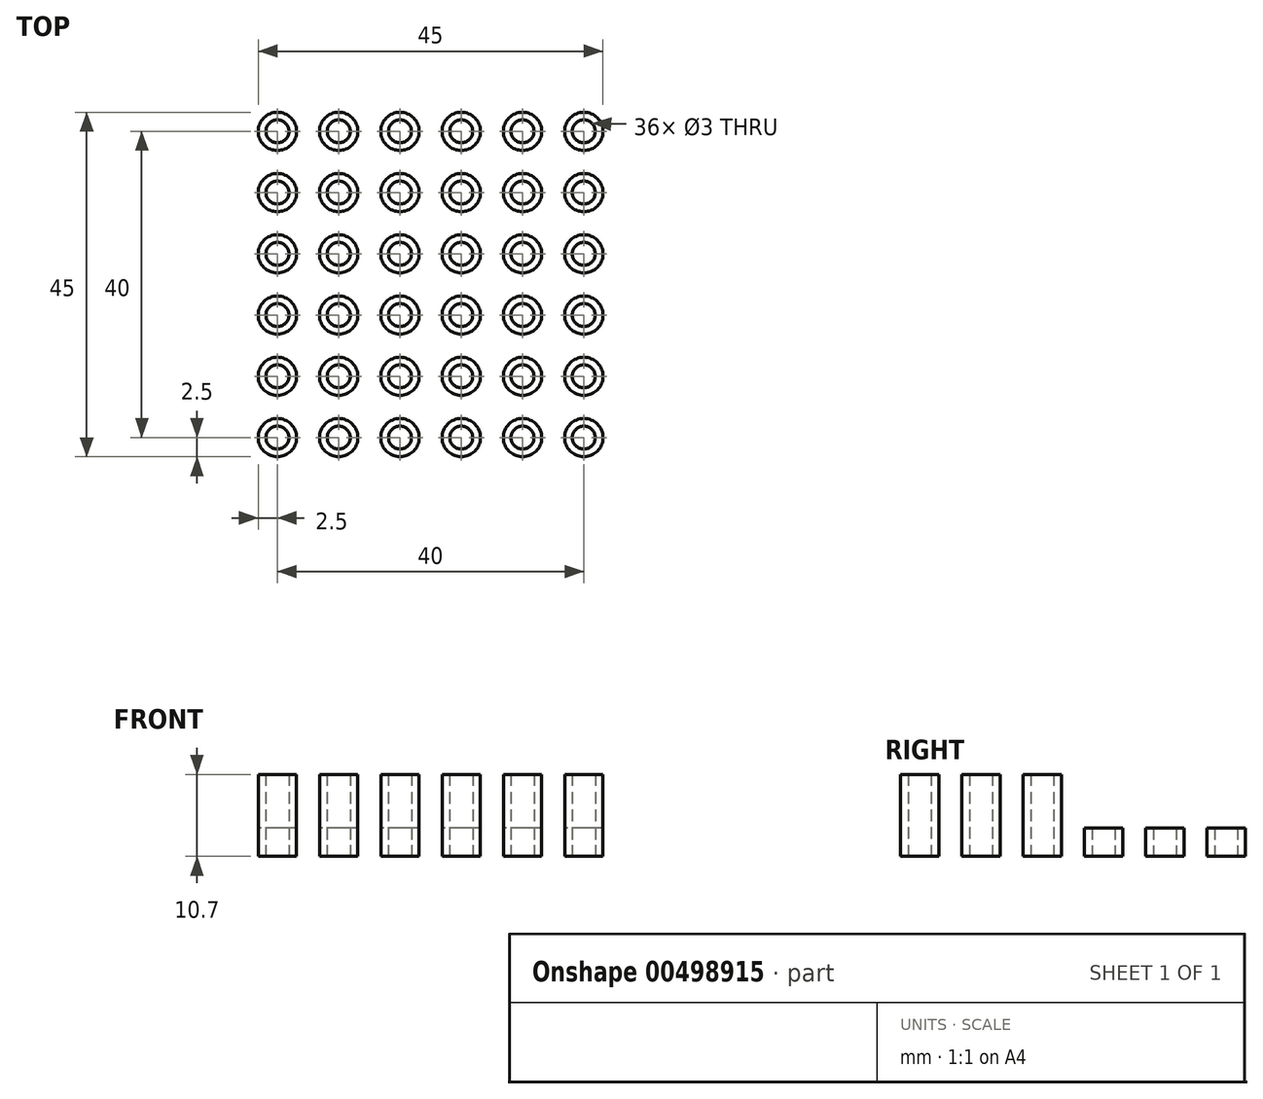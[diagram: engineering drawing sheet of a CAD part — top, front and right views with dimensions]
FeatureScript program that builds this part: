
annotation { "Feature Type Name" : "Feature", "Feature Type Description" : "" }
export const myFeature = defineFeature(function(context is Context, id is Id, definition is map)
    precondition{}
    {
        {
            var Q0;
            Q0=qCreatedBy(makeId("Top.planeOp"),FACE);
            var sketch = newSketch(context, id + "F0", { "sketchPlane" : qUnion([Q0])});
            skCircle(sketch, "E0", {"center": v(-20, -20) * mm, "radius": 1.5 * mm});
            skCircle(sketch, "E1", {"center": v(-20, -20) * mm, "radius": 2.5 * mm});
            skCircle(sketch, "E2.0.1.0", {"center": v(-20, -12) * mm, "radius": 2.5 * mm});
            skCircle(sketch, "E2.0.1.1", {"center": v(-20, -12) * mm, "radius": 1.5 * mm});
            skCircle(sketch, "E2.0.2.0", {"center": v(-20, -4) * mm, "radius": 2.5 * mm});
            skCircle(sketch, "E2.0.2.1", {"center": v(-20, -4) * mm, "radius": 1.5 * mm});
            skCircle(sketch, "E2.0.3.0", {"center": v(-20, 4) * mm, "radius": 2.5 * mm});
            skCircle(sketch, "E2.0.3.1", {"center": v(-20, 4) * mm, "radius": 1.5 * mm});
            skCircle(sketch, "E2.0.4.0", {"center": v(-20, 12) * mm, "radius": 2.5 * mm});
            skCircle(sketch, "E2.0.4.1", {"center": v(-20, 12) * mm, "radius": 1.5 * mm});
            skCircle(sketch, "E2.0.5.0", {"center": v(-20, 20) * mm, "radius": 2.5 * mm});
            skCircle(sketch, "E2.0.5.1", {"center": v(-20, 20) * mm, "radius": 1.5 * mm});
            skCircle(sketch, "E2.1.0.0", {"center": v(-12, -20) * mm, "radius": 2.5 * mm});
            skCircle(sketch, "E2.1.0.1", {"center": v(-12, -20) * mm, "radius": 1.5 * mm});
            skCircle(sketch, "E2.1.1.0", {"center": v(-12, -12) * mm, "radius": 2.5 * mm});
            skCircle(sketch, "E2.1.1.1", {"center": v(-12, -12) * mm, "radius": 1.5 * mm});
            skCircle(sketch, "E2.1.2.0", {"center": v(-12, -4) * mm, "radius": 2.5 * mm});
            skCircle(sketch, "E2.1.2.1", {"center": v(-12, -4) * mm, "radius": 1.5 * mm});
            skCircle(sketch, "E2.1.3.0", {"center": v(-12, 4) * mm, "radius": 2.5 * mm});
            skCircle(sketch, "E2.1.3.1", {"center": v(-12, 4) * mm, "radius": 1.5 * mm});
            skCircle(sketch, "E2.1.4.0", {"center": v(-12, 12) * mm, "radius": 2.5 * mm});
            skCircle(sketch, "E2.1.4.1", {"center": v(-12, 12) * mm, "radius": 1.5 * mm});
            skCircle(sketch, "E2.1.5.0", {"center": v(-12, 20) * mm, "radius": 2.5 * mm});
            skCircle(sketch, "E2.1.5.1", {"center": v(-12, 20) * mm, "radius": 1.5 * mm});
            skCircle(sketch, "E2.2.0.0", {"center": v(-4, -20) * mm, "radius": 2.5 * mm});
            skCircle(sketch, "E2.2.0.1", {"center": v(-4, -20) * mm, "radius": 1.5 * mm});
            skCircle(sketch, "E2.2.1.0", {"center": v(-4, -12) * mm, "radius": 2.5 * mm});
            skCircle(sketch, "E2.2.1.1", {"center": v(-4, -12) * mm, "radius": 1.5 * mm});
            skCircle(sketch, "E2.2.2.0", {"center": v(-4, -4) * mm, "radius": 2.5 * mm});
            skCircle(sketch, "E2.2.2.1", {"center": v(-4, -4) * mm, "radius": 1.5 * mm});
            skCircle(sketch, "E2.2.3.0", {"center": v(-4, 4) * mm, "radius": 2.5 * mm});
            skCircle(sketch, "E2.2.3.1", {"center": v(-4, 4) * mm, "radius": 1.5 * mm});
            skCircle(sketch, "E2.2.4.0", {"center": v(-4, 12) * mm, "radius": 2.5 * mm});
            skCircle(sketch, "E2.2.4.1", {"center": v(-4, 12) * mm, "radius": 1.5 * mm});
            skCircle(sketch, "E2.2.5.0", {"center": v(-4, 20) * mm, "radius": 2.5 * mm});
            skCircle(sketch, "E2.2.5.1", {"center": v(-4, 20) * mm, "radius": 1.5 * mm});
            skCircle(sketch, "E2.3.0.0", {"center": v(4, -20) * mm, "radius": 2.5 * mm});
            skCircle(sketch, "E2.3.0.1", {"center": v(4, -20) * mm, "radius": 1.5 * mm});
            skCircle(sketch, "E2.3.1.0", {"center": v(4, -12) * mm, "radius": 2.5 * mm});
            skCircle(sketch, "E2.3.1.1", {"center": v(4, -12) * mm, "radius": 1.5 * mm});
            skCircle(sketch, "E2.3.2.0", {"center": v(4, -4) * mm, "radius": 2.5 * mm});
            skCircle(sketch, "E2.3.2.1", {"center": v(4, -4) * mm, "radius": 1.5 * mm});
            skCircle(sketch, "E2.3.3.0", {"center": v(4, 4) * mm, "radius": 2.5 * mm});
            skCircle(sketch, "E2.3.3.1", {"center": v(4, 4) * mm, "radius": 1.5 * mm});
            skCircle(sketch, "E2.3.4.0", {"center": v(4, 12) * mm, "radius": 2.5 * mm});
            skCircle(sketch, "E2.3.4.1", {"center": v(4, 12) * mm, "radius": 1.5 * mm});
            skCircle(sketch, "E2.3.5.0", {"center": v(4, 20) * mm, "radius": 2.5 * mm});
            skCircle(sketch, "E2.3.5.1", {"center": v(4, 20) * mm, "radius": 1.5 * mm});
            skCircle(sketch, "E2.4.0.0", {"center": v(12, -20) * mm, "radius": 2.5 * mm});
            skCircle(sketch, "E2.4.0.1", {"center": v(12, -20) * mm, "radius": 1.5 * mm});
            skCircle(sketch, "E2.4.1.0", {"center": v(12, -12) * mm, "radius": 2.5 * mm});
            skCircle(sketch, "E2.4.1.1", {"center": v(12, -12) * mm, "radius": 1.5 * mm});
            skCircle(sketch, "E2.4.2.0", {"center": v(12, -4) * mm, "radius": 2.5 * mm});
            skCircle(sketch, "E2.4.2.1", {"center": v(12, -4) * mm, "radius": 1.5 * mm});
            skCircle(sketch, "E2.4.3.0", {"center": v(12, 4) * mm, "radius": 2.5 * mm});
            skCircle(sketch, "E2.4.3.1", {"center": v(12, 4) * mm, "radius": 1.5 * mm});
            skCircle(sketch, "E2.4.4.0", {"center": v(12, 12) * mm, "radius": 2.5 * mm});
            skCircle(sketch, "E2.4.4.1", {"center": v(12, 12) * mm, "radius": 1.5 * mm});
            skCircle(sketch, "E2.4.5.0", {"center": v(12, 20) * mm, "radius": 2.5 * mm});
            skCircle(sketch, "E2.4.5.1", {"center": v(12, 20) * mm, "radius": 1.5 * mm});
            skCircle(sketch, "E2.5.0.0", {"center": v(20, -20) * mm, "radius": 2.5 * mm});
            skCircle(sketch, "E2.5.0.1", {"center": v(20, -20) * mm, "radius": 1.5 * mm});
            skCircle(sketch, "E2.5.1.0", {"center": v(20, -12) * mm, "radius": 2.5 * mm});
            skCircle(sketch, "E2.5.1.1", {"center": v(20, -12) * mm, "radius": 1.5 * mm});
            skCircle(sketch, "E2.5.2.0", {"center": v(20, -4) * mm, "radius": 2.5 * mm});
            skCircle(sketch, "E2.5.2.1", {"center": v(20, -4) * mm, "radius": 1.5 * mm});
            skCircle(sketch, "E2.5.3.0", {"center": v(20, 4) * mm, "radius": 2.5 * mm});
            skCircle(sketch, "E2.5.3.1", {"center": v(20, 4) * mm, "radius": 1.5 * mm});
            skCircle(sketch, "E2.5.4.0", {"center": v(20, 12) * mm, "radius": 2.5 * mm});
            skCircle(sketch, "E2.5.4.1", {"center": v(20, 12) * mm, "radius": 1.5 * mm});
            skCircle(sketch, "E2.5.5.0", {"center": v(20, 20) * mm, "radius": 2.5 * mm});
            skCircle(sketch, "E2.5.5.1", {"center": v(20, 20) * mm, "radius": 1.5 * mm});
            skLineSegment(sketch, "E2.direction1", {"start": v(-20, -20) * mm, "end": v(-12, -20) * mm, "construction": true});
            skLineSegment(sketch, "E2.direction2", {"start": v(-20, -20) * mm, "end": v(-20, -12) * mm, "construction": true});
            skSolve(sketch);
        }
        {
            var Q0;
            Q0=makeQuery(id+"F0.imprint","IMPRINT",FACE,{"disambiguationData":[TD([[makeQuery(id+"F0.imprint","IMPRINT",EDGE,{"derivedFrom":sQuery(id+"F0.wireOp",EDGE,"E2.0.5.0")}),1.0]])]});
            var Q1;
            Q1=makeQuery(id+"F0.imprint","IMPRINT",FACE,{"disambiguationData":[TD([[makeQuery(id+"F0.imprint","IMPRINT",EDGE,{"derivedFrom":sQuery(id+"F0.wireOp",EDGE,"E2.2.5.0")}),1.0]])]});
            var Q2;
            Q2=makeQuery(id+"F0.imprint","IMPRINT",FACE,{"disambiguationData":[TD([[makeQuery(id+"F0.imprint","IMPRINT",EDGE,{"derivedFrom":sQuery(id+"F0.wireOp",EDGE,"E2.1.5.0")}),1.0]])]});
            var Q3;
            Q3=makeQuery(id+"F0.imprint","IMPRINT",FACE,{"disambiguationData":[TD([[makeQuery(id+"F0.imprint","IMPRINT",EDGE,{"derivedFrom":sQuery(id+"F0.wireOp",EDGE,"E2.3.5.0")}),1.0]])]});
            var Q4;
            Q4=makeQuery(id+"F0.imprint","IMPRINT",FACE,{"disambiguationData":[TD([[makeQuery(id+"F0.imprint","IMPRINT",EDGE,{"derivedFrom":sQuery(id+"F0.wireOp",EDGE,"E2.4.5.0")}),1.0]])]});
            var Q5;
            Q5=makeQuery(id+"F0.imprint","IMPRINT",FACE,{"disambiguationData":[TD([[makeQuery(id+"F0.imprint","IMPRINT",EDGE,{"derivedFrom":sQuery(id+"F0.wireOp",EDGE,"E2.4.4.0")}),1.0]])]});
            var Q6;
            Q6=makeQuery(id+"F0.imprint","IMPRINT",FACE,{"disambiguationData":[TD([[makeQuery(id+"F0.imprint","IMPRINT",EDGE,{"derivedFrom":sQuery(id+"F0.wireOp",EDGE,"E2.3.4.0")}),1.0]])]});
            var Q7;
            Q7=makeQuery(id+"F0.imprint","IMPRINT",FACE,{"disambiguationData":[TD([[makeQuery(id+"F0.imprint","IMPRINT",EDGE,{"derivedFrom":sQuery(id+"F0.wireOp",EDGE,"E2.2.4.0")}),1.0]])]});
            var Q8;
            Q8=makeQuery(id+"F0.imprint","IMPRINT",FACE,{"disambiguationData":[TD([[makeQuery(id+"F0.imprint","IMPRINT",EDGE,{"derivedFrom":sQuery(id+"F0.wireOp",EDGE,"E2.1.4.0")}),1.0]])]});
            var Q9;
            Q9=makeQuery(id+"F0.imprint","IMPRINT",FACE,{"disambiguationData":[TD([[makeQuery(id+"F0.imprint","IMPRINT",EDGE,{"derivedFrom":sQuery(id+"F0.wireOp",EDGE,"E2.5.5.0")}),1.0]])]});
            var Q10;
            Q10=makeQuery(id+"F0.imprint","IMPRINT",FACE,{"disambiguationData":[TD([[makeQuery(id+"F0.imprint","IMPRINT",EDGE,{"derivedFrom":sQuery(id+"F0.wireOp",EDGE,"E2.5.4.0")}),1.0]])]});
            var Q11;
            Q11=makeQuery(id+"F0.imprint","IMPRINT",FACE,{"disambiguationData":[TD([[makeQuery(id+"F0.imprint","IMPRINT",EDGE,{"derivedFrom":sQuery(id+"F0.wireOp",EDGE,"E2.0.4.0")}),1.0]])]});
            var Q12;
            Q12=makeQuery(id+"F0.imprint","IMPRINT",FACE,{"disambiguationData":[TD([[makeQuery(id+"F0.imprint","IMPRINT",EDGE,{"derivedFrom":sQuery(id+"F0.wireOp",EDGE,"E2.0.3.0")}),1.0]])]});
            var Q13;
            Q13=makeQuery(id+"F0.imprint","IMPRINT",FACE,{"disambiguationData":[TD([[makeQuery(id+"F0.imprint","IMPRINT",EDGE,{"derivedFrom":sQuery(id+"F0.wireOp",EDGE,"E2.1.3.0")}),1.0]])]});
            var Q14;
            Q14=makeQuery(id+"F0.imprint","IMPRINT",FACE,{"disambiguationData":[TD([[makeQuery(id+"F0.imprint","IMPRINT",EDGE,{"derivedFrom":sQuery(id+"F0.wireOp",EDGE,"E2.2.3.0")}),1.0]])]});
            var Q15;
            Q15=makeQuery(id+"F0.imprint","IMPRINT",FACE,{"disambiguationData":[TD([[makeQuery(id+"F0.imprint","IMPRINT",EDGE,{"derivedFrom":sQuery(id+"F0.wireOp",EDGE,"E2.3.3.0")}),1.0]])]});
            var Q16;
            Q16=makeQuery(id+"F0.imprint","IMPRINT",FACE,{"disambiguationData":[TD([[makeQuery(id+"F0.imprint","IMPRINT",EDGE,{"derivedFrom":sQuery(id+"F0.wireOp",EDGE,"E2.4.3.0")}),1.0]])]});
            var Q17;
            Q17=makeQuery(id+"F0.imprint","IMPRINT",FACE,{"disambiguationData":[TD([[makeQuery(id+"F0.imprint","IMPRINT",EDGE,{"derivedFrom":sQuery(id+"F0.wireOp",EDGE,"E2.5.3.0")}),1.0]])]});
            extrude(context, id + "F1", {"entities" : qUnion([Q0, Q1, Q2, Q3, Q4, Q5, Q6, Q7, Q8, Q9, Q10, Q11, Q12, Q13, Q14, Q15, Q16, Q17]), "depth" : 3.7 * mm, "offsetDistance" : 25 * mm});
        }
        {
            var Q0;
            Q0=makeQuery(id+"F0.imprint","IMPRINT",FACE,{"disambiguationData":[TD([[makeQuery(id+"F0.imprint","IMPRINT",EDGE,{"derivedFrom":sQuery(id+"F0.wireOp",EDGE,"E2.0.2.0")}),1.0]])]});
            var Q1;
            Q1=makeQuery(id+"F0.imprint","IMPRINT",FACE,{"disambiguationData":[TD([[makeQuery(id+"F0.imprint","IMPRINT",EDGE,{"derivedFrom":sQuery(id+"F0.wireOp",EDGE,"E2.1.2.0")}),1.0]])]});
            var Q2;
            Q2=makeQuery(id+"F0.imprint","IMPRINT",FACE,{"disambiguationData":[TD([[makeQuery(id+"F0.imprint","IMPRINT",EDGE,{"derivedFrom":sQuery(id+"F0.wireOp",EDGE,"E2.2.2.0")}),1.0]])]});
            var Q3;
            Q3=makeQuery(id+"F0.imprint","IMPRINT",FACE,{"disambiguationData":[TD([[makeQuery(id+"F0.imprint","IMPRINT",EDGE,{"derivedFrom":sQuery(id+"F0.wireOp",EDGE,"E2.3.2.0")}),1.0]])]});
            var Q4;
            Q4=makeQuery(id+"F0.imprint","IMPRINT",FACE,{"disambiguationData":[TD([[makeQuery(id+"F0.imprint","IMPRINT",EDGE,{"derivedFrom":sQuery(id+"F0.wireOp",EDGE,"E2.4.2.0")}),1.0]])]});
            var Q5;
            Q5=makeQuery(id+"F0.imprint","IMPRINT",FACE,{"disambiguationData":[TD([[makeQuery(id+"F0.imprint","IMPRINT",EDGE,{"derivedFrom":sQuery(id+"F0.wireOp",EDGE,"E2.5.2.0")}),1.0]])]});
            var Q6;
            Q6=makeQuery(id+"F0.imprint","IMPRINT",FACE,{"disambiguationData":[TD([[makeQuery(id+"F0.imprint","IMPRINT",EDGE,{"derivedFrom":sQuery(id+"F0.wireOp",EDGE,"E2.5.1.0")}),1.0]])]});
            var Q7;
            Q7=makeQuery(id+"F0.imprint","IMPRINT",FACE,{"disambiguationData":[TD([[makeQuery(id+"F0.imprint","IMPRINT",EDGE,{"derivedFrom":sQuery(id+"F0.wireOp",EDGE,"E2.4.1.0")}),1.0]])]});
            var Q8;
            Q8=makeQuery(id+"F0.imprint","IMPRINT",FACE,{"disambiguationData":[TD([[makeQuery(id+"F0.imprint","IMPRINT",EDGE,{"derivedFrom":sQuery(id+"F0.wireOp",EDGE,"E2.2.1.0")}),1.0]])]});
            var Q9;
            Q9=makeQuery(id+"F0.imprint","IMPRINT",FACE,{"disambiguationData":[TD([[makeQuery(id+"F0.imprint","IMPRINT",EDGE,{"derivedFrom":sQuery(id+"F0.wireOp",EDGE,"E2.1.1.0")}),1.0]])]});
            var Q10;
            Q10=makeQuery(id+"F0.imprint","IMPRINT",FACE,{"disambiguationData":[TD([[makeQuery(id+"F0.imprint","IMPRINT",EDGE,{"derivedFrom":sQuery(id+"F0.wireOp",EDGE,"E2.0.1.0")}),1.0]])]});
            var Q11;
            Q11=makeQuery(id+"F0.imprint","IMPRINT",FACE,{"disambiguationData":[TD([[makeQuery(id+"F0.imprint","IMPRINT",EDGE,{"derivedFrom":sQuery(id+"F0.wireOp",EDGE,"E0")}),-1.0]])]});
            var Q12;
            Q12=makeQuery(id+"F0.imprint","IMPRINT",FACE,{"disambiguationData":[TD([[makeQuery(id+"F0.imprint","IMPRINT",EDGE,{"derivedFrom":sQuery(id+"F0.wireOp",EDGE,"E2.1.0.0")}),1.0]])]});
            var Q13;
            Q13=makeQuery(id+"F0.imprint","IMPRINT",FACE,{"disambiguationData":[TD([[makeQuery(id+"F0.imprint","IMPRINT",EDGE,{"derivedFrom":sQuery(id+"F0.wireOp",EDGE,"E2.2.0.0")}),1.0]])]});
            var Q14;
            Q14=makeQuery(id+"F0.imprint","IMPRINT",FACE,{"disambiguationData":[TD([[makeQuery(id+"F0.imprint","IMPRINT",EDGE,{"derivedFrom":sQuery(id+"F0.wireOp",EDGE,"E2.3.0.0")}),1.0]])]});
            var Q15;
            Q15=makeQuery(id+"F0.imprint","IMPRINT",FACE,{"disambiguationData":[TD([[makeQuery(id+"F0.imprint","IMPRINT",EDGE,{"derivedFrom":sQuery(id+"F0.wireOp",EDGE,"E2.4.0.0")}),1.0]])]});
            var Q16;
            Q16=makeQuery(id+"F0.imprint","IMPRINT",FACE,{"disambiguationData":[TD([[makeQuery(id+"F0.imprint","IMPRINT",EDGE,{"derivedFrom":sQuery(id+"F0.wireOp",EDGE,"E2.5.0.0")}),1.0]])]});
            var Q17;
            Q17=makeQuery(id+"F0.imprint","IMPRINT",FACE,{"disambiguationData":[TD([[makeQuery(id+"F0.imprint","IMPRINT",EDGE,{"derivedFrom":sQuery(id+"F0.wireOp",EDGE,"E2.3.1.0")}),1.0]])]});
            extrude(context, id + "F2", {"entities" : qUnion([Q0, Q1, Q2, Q3, Q4, Q5, Q6, Q7, Q8, Q9, Q10, Q11, Q12, Q13, Q14, Q15, Q16, Q17]), "depth" : 10.7 * mm, "offsetDistance" : 25 * mm});
        }
    });
